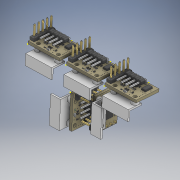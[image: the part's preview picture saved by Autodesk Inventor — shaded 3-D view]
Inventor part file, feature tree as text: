
AUTODESK INVENTOR PART (.ipt)
format: ipt  version: 2020 (Build 240168000, 168)  size: 19,605,504 bytes
history: native  units: mm
features: other x11, sketch x10
ambient origin geometry x8: Origin, YZ Plane, XZ Plane, XY Plane, X Axis, Y Axis, Z Axis, Center Point
bodies: Solid1 (feature_tree)
feature tree (21):
  other  "DržačiSaSenzorimaUdaljenosti_v.1.0.iam"
  other  "DržačSenzoraUdaljenostiOnlyOne(1)_v.1.0.ipt:1"
  other  "DržačSenzoraUdaljenostiOnlyOne(1)_v.1.0.ipt:2"
  other  "DržačSenzoraUdaljenostiOnlyOne(1)_v.1.0.ipt:3"
  other  "mrm-lid-an.ipt:1"
  other  "mrm-lid-an.ipt:2"
  other  "mrm-lid-an.ipt:3"
  other  "mrm-lid-an.ipt:4"
  other  "mrm-lid-an.ipt:5"
  other  "DržačSenzoraUdaljenostiOnlyOne(1)_v.1.0.ipt:4"
  other  "DržačSenzoraUdaljenostiOnlyOne(1)_v.1.0.ipt:5"
  sketch  "Sketch8"
  sketch  "Sketch8_1"  dims[d0=10.0mm]
  sketch  "Sketch8_2"
  sketch  "Sketch1"
  sketch  "Sketch1_1"
  sketch  "Sketch1_2"
  sketch  "Sketch1_3"
  sketch  "Sketch1_4"
  sketch  "Sketch8_3"
  sketch  "Sketch8_4"
